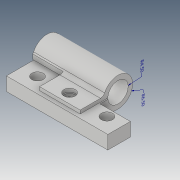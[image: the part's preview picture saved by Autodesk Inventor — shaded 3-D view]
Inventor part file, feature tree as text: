
AUTODESK INVENTOR PART (.ipt)
format: ipt  version: 2019 (Build 230136000, 136)  size: 242,176 bytes
history: native  units: mm
features: extrude x11, sketch x9, plane x4, other x3, fillet x2, move_body x2, direct_edit x1, projected_geometry x1
ambient origin geometry x8: Origin, YZ Plane, XZ Plane, XY Plane, X Axis, Y Axis, Z Axis, Center Point
bodies: Solid1 (feature_tree)
feature tree (33):
  other  "Annotations"
  extrude  "Extrusion1"  Depth=45.0mm
  extrude  "Extrusion4"  Depth=5.0mm
  fillet  "Fillet1"  Radius=11.0mm
  extrude  "Extrusion5"  Depth=23.0mm
  plane  "Work Plane1"
  extrude  "Extrusion6"  Depth=10.0mm
  direct_edit  "Direct Edit1"
  extrude  "Extrusion7"  Depth=12.0mm
  fillet  "Fillet2"  Radius=5.0mm
  plane  "Work Plane5"
  extrude  "Extrusion8"  Depth=5.0mm
  plane  "Work Plane6"
  extrude  "Extrusion9"  Depth=5.0mm
  sketch  "Sketch12"  dims[d34=5.0mm d35=17.8mm]
  extrude  "Extrusion12"  Depth=8.0mm
  extrude  "Extrusion13"  Depth=4.5mm
  extrude  "Extrusion15"  Depth=4.5mm
  plane  "Work Plane7"
  extrude  "Extrusion16"  Depth=4.5mm TaperAngle=0.0deg
  sketch  "Sketch1"  dims[d0=6.0mm d1=0.0mm d4=45.0mm]
  sketch  "Sketch5"  dims[d5=5.0mm d6=5.0mm d7=11.0mm]
  sketch  "Sketch6"  dims[d8=11.0mm d9=23.0mm]
  sketch  "Sketch7"  dims[d10=10.0mm d20=13.0mm]
  sketch  "Sketch8"  dims[d24=3.0mm d25=0.0mm d26=12.0mm d27=5.0mm]
  sketch  "Sketch10"  dims[d28=3.0mm d29=0.0mm d33=5.0mm]
  projected_geometry  "Projected Loop2"
  sketch  "Sketch13"  dims[d36=8.0mm d37=17.8mm]
  sketch  "Sketch14"  dims[d38=7.1mm d39=30.8mm d40=7.1mm d41=3.0mm d42=0.0mm d46=0.0mm d47=0.0mm d48=-2.5mm d49=0.0mm d50=0.0mm d51=-2.5mm d52=18.0mm d53=11.0mm d54=2.0mm d55=0.0mm d56=2.0mm d57=0.0mm d58=0.5mm d59=0.0mm d60=0.0mm d61=7.25mm d62=0.0mm d68=5.0mm d69=7.25mm d70=0.0mm d72=2.0mm d73=10.0mm d74=0.0mm d80=10.0mm d81=0.0mm d82=15.0mm d83=3.0mm d88=-4.5mm d89=7.5mm d90=3.15mm d91=0.0mm d84=49.911908mm d85=6.5mm d86=52.109261mm d87=4.5mm]
  move_body  "Move1"
  move_body  "Move2"
  other  "Radial Dimension 1"
  other  "Radial Dimension 2"
